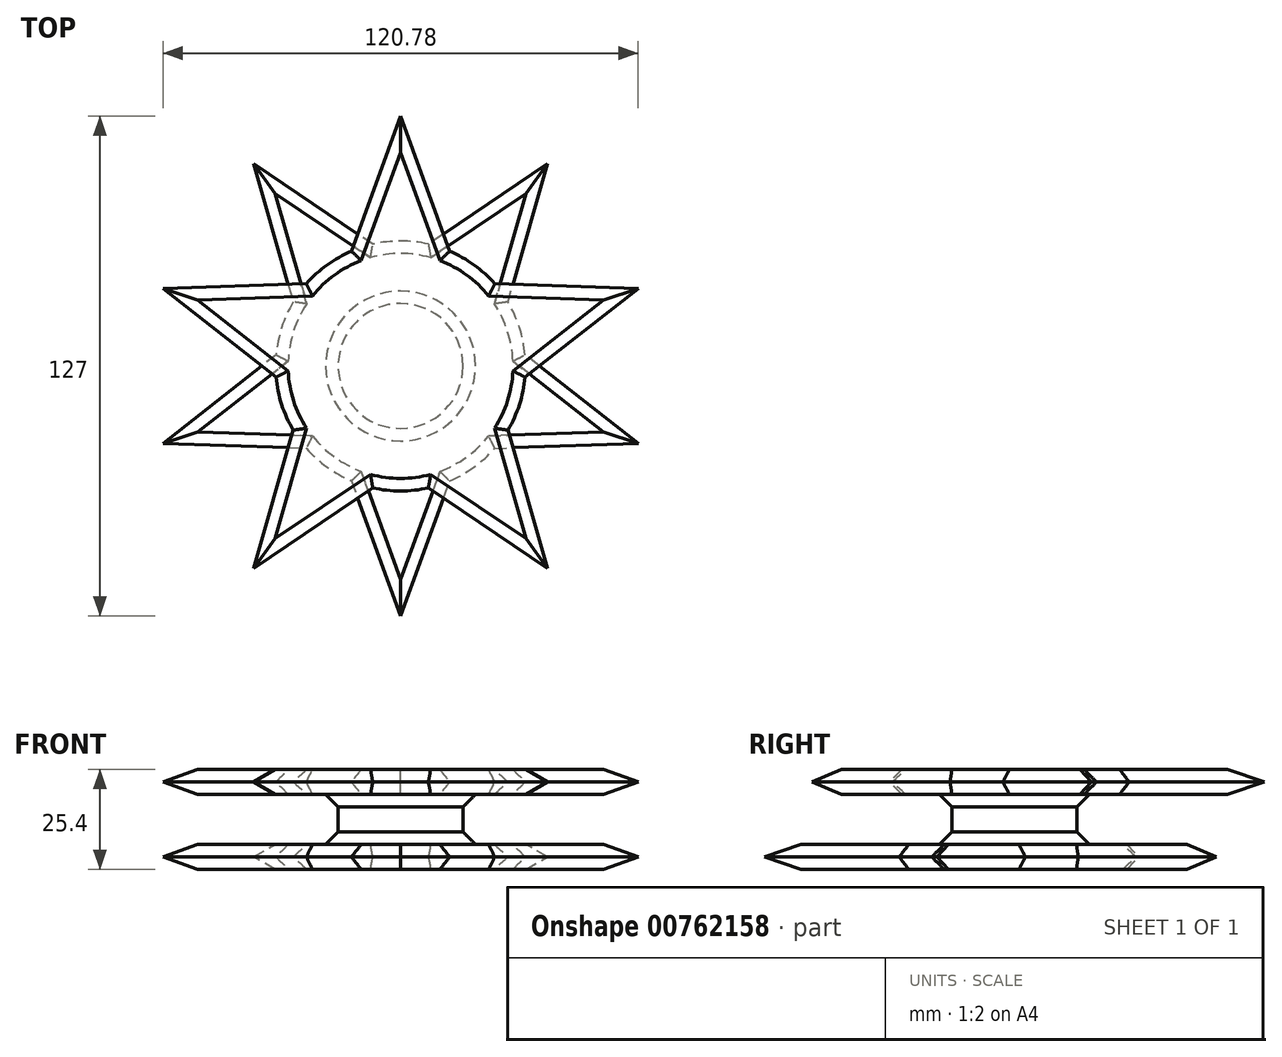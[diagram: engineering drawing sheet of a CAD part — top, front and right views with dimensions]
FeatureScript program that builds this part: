
annotation { "Feature Type Name" : "Feature", "Feature Type Description" : "" }
export const myFeature = defineFeature(function(context is Context, id is Id, definition is map)
    precondition{}
    {
        {
            var Q0;
            Q0=qCreatedBy(makeId("Top.planeOp"),FACE);
            var sketch = newSketch(context, id + "F0", { "sketchPlane" : qUnion([Q0])});
            skCircle(sketch, "E0", {"center": v(0, 0) * mm, "radius": 31.75 * mm});
            skSolve(sketch);
        }
        {
            var Q0;
            Q0 = qSketchRegion(id + "F0", true);
            extrude(context, id + "F1", {"entities" : qUnion([Q0]), "endBound" : BoundingType.SYMMETRIC, "depth" : 25.4 * mm, "offsetDistance" : 25.4 * mm});
        }
        {
            var Q0;
            Q0=qCreatedBy(makeId("Front.planeOp"),FACE);
            var sketch = newSketch(context, id + "F2", { "sketchPlane" : qUnion([Q0])});
            skLineSegment(sketch, "E1", {"start": v(15.88, 6.35) * mm, "end": v(31.75, 6.35) * mm});
            skLineSegment(sketch, "E2.MirrorCS", {"start": v(15.88, -6.35) * mm, "end": v(31.75, -6.35) * mm});
            skLineSegment(sketch, "E3", {"start": v(15.88, 6.35) * mm, "end": v(15.88, -6.35) * mm});
            skPoint(sketch, "E4.orphan", {"position": v(0, -6.35) * mm});
            skPoint(sketch, "E5.MirrorCS.start.orphan", {"position": v(0, 0) * mm});
            skPoint(sketch, "E6.end.orphan", {"position": v(0, 6.35) * mm});
            skPoint(sketch, "E7.start.orphan", {"position": v(31.75, 0) * mm});
            skPoint(sketch, "E8.orphan", {"position": v(31.75, 12.7) * mm});
            skPoint(sketch, "E9.orphan", {"position": v(31.75, -12.7) * mm});
            skLineSegment(sketch, "E10", {"start": v(31.75, 6.35) * mm, "end": v(33.28, 6.35) * mm});
            skLineSegment(sketch, "E11", {"start": v(33.28, 6.35) * mm, "end": v(33.28, -6.35) * mm});
            skLineSegment(sketch, "E12", {"start": v(33.28, -6.35) * mm, "end": v(31.75, -6.35) * mm});
            skLineSegment(sketch, "E13", {"start": v(0, 0) * mm, "end": v(0, 6.35) * mm});
            skSolve(sketch);
        }
        {
            var Q0;
            Q0 = qSketchRegion(id + "F2", true);
            var Q1;
            Q1=sQuery(id+"F2.wireOp",EDGE,"E13");
            revolve(context, id + "F3", {"operationType" : NewBodyOperationType.REMOVE, "surfaceOperationType" : NewSurfaceOperationType.NEW, "entities" : qUnion([Q0]), "axis" : qUnion([Q1]), "revolveType" : RevolveType.FULL, "oppositeDirection" : true});
        }
        {
            var Q0;
            Q0=makeQuery(id+"F1.opExtrude","CAP_FACE",FACE,{"disambiguationData":[OSD([sQuery(id+"F0.wireOp",EDGE,"E0")])],"isStart":false});
            var sketch = newSketch(context, id + "F4", { "sketchPlane" : qUnion([Q0])});
            skCircle(sketch, "E14", {"center": v(0, 0) * mm, "radius": 31.75 * mm});
            skLineSegment(sketch, "E15", {"start": v(0, 0) * mm, "end": v(0, 63.5) * mm});
            skLineSegment(sketch, "E16", {"start": v(0, 63.5) * mm, "end": v(-12.49, 29.2) * mm});
            skLineSegment(sketch, "E17", {"start": v(0, 63.5) * mm, "end": v(12.49, 29.2) * mm});
            skLineSegment(sketch, "E18.1.0", {"start": v(-60.4, 19.62) * mm, "end": v(-31.62, -2.86) * mm});
            skLineSegment(sketch, "E18.1.1", {"start": v(-60.4, 19.62) * mm, "end": v(-23.9, 20.9) * mm});
            skLineSegment(sketch, "E18.2.0", {"start": v(-37.32, -51.37) * mm, "end": v(-7.06, -30.96) * mm});
            skLineSegment(sketch, "E18.2.1", {"start": v(-37.32, -51.37) * mm, "end": v(-27.26, -16.28) * mm});
            skLineSegment(sketch, "E18.3.0", {"start": v(37.32, -51.37) * mm, "end": v(27.26, -16.28) * mm});
            skLineSegment(sketch, "E18.3.1", {"start": v(37.32, -51.37) * mm, "end": v(7.06, -30.96) * mm});
            skLineSegment(sketch, "E18.4.0", {"start": v(60.4, 19.62) * mm, "end": v(23.9, 20.9) * mm});
            skLineSegment(sketch, "E18.4.1", {"start": v(60.4, 19.62) * mm, "end": v(31.62, -2.86) * mm});
            skSolve(sketch);
        }
        {
            var Q0;
            {var subQ0=sQuery(id+"F4.wireOp",EDGE,"E17");Q0=makeQuery(id+"F4.imprint","IMPRINT",FACE,{"disambiguationData":[TD([[makeQuery(id+"F4.imprint","IMPRINT",EDGE,{"derivedFrom":subQ0}),-1.0]])]});}
            var Q1;
            {var subQ0=sQuery(id+"F4.wireOp",EDGE,"E16");Q1=makeQuery(id+"F4.imprint","IMPRINT",FACE,{"disambiguationData":[TD([[makeQuery(id+"F4.imprint","IMPRINT",EDGE,{"derivedFrom":subQ0}),1.0]])]});}
            var Q2;
            {var subQ0=sQuery(id+"F4.wireOp",EDGE,"E18.1.0");Q2=makeQuery(id+"F4.imprint","IMPRINT",FACE,{"disambiguationData":[TD([[makeQuery(id+"F4.imprint","IMPRINT",EDGE,{"derivedFrom":subQ0}),1.0]])]});}
            var Q3;
            {var subQ0=sQuery(id+"F4.wireOp",EDGE,"E18.2.0");Q3=makeQuery(id+"F4.imprint","IMPRINT",FACE,{"disambiguationData":[TD([[makeQuery(id+"F4.imprint","IMPRINT",EDGE,{"derivedFrom":subQ0}),1.0]])]});}
            var Q4;
            {var subQ0=sQuery(id+"F4.wireOp",EDGE,"E18.3.0");Q4=makeQuery(id+"F4.imprint","IMPRINT",FACE,{"disambiguationData":[TD([[makeQuery(id+"F4.imprint","IMPRINT",EDGE,{"derivedFrom":subQ0}),1.0]])]});}
            var Q5;
            {var subQ0=sQuery(id+"F4.wireOp",EDGE,"E18.4.0");Q5=makeQuery(id+"F4.imprint","IMPRINT",FACE,{"disambiguationData":[TD([[makeQuery(id+"F4.imprint","IMPRINT",EDGE,{"derivedFrom":subQ0}),1.0]])]});}
            extrude(context, id + "F5", {"entities" : qUnion([Q0, Q1, Q2, Q3, Q4, Q5]), "operationType" : NewBodyOperationType.ADD, "oppositeDirection" : true, "depth" : 6.35 * mm, "offsetDistance" : 25.4 * mm});
        }
        {
            var Q0;
            Q0=makeQuery(id+"F1.opExtrude","CAP_FACE",FACE,{"disambiguationData":[OSD([sQuery(id+"F0.wireOp",EDGE,"E0")])],"isStart":true});
            var sketch = newSketch(context, id + "F6", { "sketchPlane" : qUnion([Q0])});
            skCircle(sketch, "E19.0", {"center": v(0, 0) * mm, "radius": 31.75 * mm});
            skLineSegment(sketch, "E20", {"start": v(0, 0) * mm, "end": v(0, 63.5) * mm});
            skLineSegment(sketch, "E21", {"start": v(0, 63.5) * mm, "end": v(-12.49, 29.2) * mm});
            skLineSegment(sketch, "E22", {"start": v(0, 63.5) * mm, "end": v(12.49, 29.2) * mm});
            skLineSegment(sketch, "E23.1.0", {"start": v(-60.4, 19.62) * mm, "end": v(-31.62, -2.86) * mm});
            skLineSegment(sketch, "E23.1.1", {"start": v(-60.4, 19.62) * mm, "end": v(-23.9, 20.9) * mm});
            skLineSegment(sketch, "E23.2.0", {"start": v(-37.32, -51.37) * mm, "end": v(-7.06, -30.96) * mm});
            skLineSegment(sketch, "E23.2.1", {"start": v(-37.32, -51.37) * mm, "end": v(-27.26, -16.28) * mm});
            skLineSegment(sketch, "E23.3.0", {"start": v(37.32, -51.37) * mm, "end": v(27.26, -16.28) * mm});
            skLineSegment(sketch, "E23.3.1", {"start": v(37.32, -51.37) * mm, "end": v(7.06, -30.96) * mm});
            skLineSegment(sketch, "E23.4.0", {"start": v(60.4, 19.62) * mm, "end": v(23.9, 20.9) * mm});
            skLineSegment(sketch, "E23.4.1", {"start": v(60.4, 19.62) * mm, "end": v(31.62, -2.86) * mm});
            skSolve(sketch);
        }
        {
            var Q0;
            {var subQ0=sQuery(id+"F6.wireOp",EDGE,"E21");Q0=makeQuery(id+"F6.imprint","IMPRINT",FACE,{"disambiguationData":[TD([[makeQuery(id+"F6.imprint","IMPRINT",EDGE,{"derivedFrom":subQ0}),1.0]])]});}
            var Q1;
            {var subQ0=sQuery(id+"F6.wireOp",EDGE,"E22");Q1=makeQuery(id+"F6.imprint","IMPRINT",FACE,{"disambiguationData":[TD([[makeQuery(id+"F6.imprint","IMPRINT",EDGE,{"derivedFrom":subQ0}),-1.0]])]});}
            var Q2;
            {var subQ0=sQuery(id+"F6.wireOp",EDGE,"E23.1.0");Q2=makeQuery(id+"F6.imprint","IMPRINT",FACE,{"disambiguationData":[TD([[makeQuery(id+"F6.imprint","IMPRINT",EDGE,{"derivedFrom":subQ0}),1.0]])]});}
            var Q3;
            {var subQ0=sQuery(id+"F6.wireOp",EDGE,"E23.4.0");Q3=makeQuery(id+"F6.imprint","IMPRINT",FACE,{"disambiguationData":[TD([[makeQuery(id+"F6.imprint","IMPRINT",EDGE,{"derivedFrom":subQ0}),1.0]])]});}
            var Q4;
            {var subQ0=sQuery(id+"F6.wireOp",EDGE,"E23.2.0");Q4=makeQuery(id+"F6.imprint","IMPRINT",FACE,{"disambiguationData":[TD([[makeQuery(id+"F6.imprint","IMPRINT",EDGE,{"derivedFrom":subQ0}),1.0]])]});}
            var Q5;
            {var subQ0=sQuery(id+"F6.wireOp",EDGE,"E23.3.0");Q5=makeQuery(id+"F6.imprint","IMPRINT",FACE,{"disambiguationData":[TD([[makeQuery(id+"F6.imprint","IMPRINT",EDGE,{"derivedFrom":subQ0}),1.0]])]});}
            extrude(context, id + "F7", {"entities" : qUnion([Q0, Q1, Q2, Q3, Q4, Q5]), "operationType" : NewBodyOperationType.ADD, "oppositeDirection" : true, "depth" : 6.35 * mm, "offsetDistance" : 25.4 * mm});
        }
        {
            var Q0;
            {var subQ0=sQuery(id+"F4.wireOp",EDGE,"E14");Q0=makeQuery(id+"F5.boolean.opBoolean","MERGE",FACE,{"derivedFrom":[makeQuery(id+"F1.opExtrude","CAP_FACE",FACE,{"disambiguationData":[OSD([sQuery(id+"F0.wireOp",EDGE,"E0")])],"isStart":false}),makeQuery(id+"F5.opExtrude","CAP_FACE",FACE,{"disambiguationData":[OSD([subQ0,sQuery(id+"F4.wireOp",EDGE,"E16"),sQuery(id+"F4.wireOp",EDGE,"E17")])],"isStart":true}),makeQuery(id+"F5.opExtrude","CAP_FACE",FACE,{"disambiguationData":[OSD([subQ0,sQuery(id+"F4.wireOp",EDGE,"E18.1.0"),sQuery(id+"F4.wireOp",EDGE,"E18.1.1")])],"isStart":true}),makeQuery(id+"F5.opExtrude","CAP_FACE",FACE,{"disambiguationData":[OSD([subQ0,sQuery(id+"F4.wireOp",EDGE,"E18.2.0"),sQuery(id+"F4.wireOp",EDGE,"E18.2.1")])],"isStart":true}),makeQuery(id+"F5.opExtrude","CAP_FACE",FACE,{"disambiguationData":[OSD([subQ0,sQuery(id+"F4.wireOp",EDGE,"E18.3.0"),sQuery(id+"F4.wireOp",EDGE,"E18.3.1")])],"isStart":true}),makeQuery(id+"F5.opExtrude","CAP_FACE",FACE,{"disambiguationData":[OSD([subQ0,sQuery(id+"F4.wireOp",EDGE,"E18.4.0"),sQuery(id+"F4.wireOp",EDGE,"E18.4.1")])],"isStart":true})]});}
            var Q1;
            {var subQ0=sQuery(id+"F6.wireOp",EDGE,"E19.0");Q1=makeQuery(id+"F7.boolean.opBoolean","MERGE",FACE,{"derivedFrom":[makeQuery(id+"F3.boolean.opBoolean","COPY",FACE,{"derivedFrom":makeQuery(id+"F3.opRevolve","SWEPT_FACE",FACE,{"disambiguationData":[OSD([sQuery(id+"F2.wireOp",EDGE,"E2.MirrorCS"),sQuery(id+"F2.wireOp",EDGE,"E12")])]})}),makeQuery(id+"F7.opExtrude","CAP_FACE",FACE,{"disambiguationData":[OSD([subQ0,sQuery(id+"F6.wireOp",EDGE,"E23.3.0"),sQuery(id+"F6.wireOp",EDGE,"E23.3.1")])],"isStart":false}),makeQuery(id+"F7.opExtrude","CAP_FACE",FACE,{"disambiguationData":[OSD([subQ0,sQuery(id+"F6.wireOp",EDGE,"E23.2.0"),sQuery(id+"F6.wireOp",EDGE,"E23.2.1")])],"isStart":false}),makeQuery(id+"F7.opExtrude","CAP_FACE",FACE,{"disambiguationData":[OSD([subQ0,sQuery(id+"F6.wireOp",EDGE,"E23.1.0"),sQuery(id+"F6.wireOp",EDGE,"E23.1.1")])],"isStart":false}),makeQuery(id+"F7.opExtrude","CAP_FACE",FACE,{"disambiguationData":[OSD([subQ0,sQuery(id+"F6.wireOp",EDGE,"E21"),sQuery(id+"F6.wireOp",EDGE,"E22")])],"isStart":false}),makeQuery(id+"F7.opExtrude","CAP_FACE",FACE,{"disambiguationData":[OSD([subQ0,sQuery(id+"F6.wireOp",EDGE,"E23.4.0"),sQuery(id+"F6.wireOp",EDGE,"E23.4.1")])],"isStart":false})]});}
            var Q2;
            {var subQ0=sQuery(id+"F4.wireOp",EDGE,"E14");Q2=makeQuery(id+"F5.boolean.opBoolean","MERGE",FACE,{"derivedFrom":[makeQuery(id+"F3.boolean.opBoolean","COPY",FACE,{"derivedFrom":makeQuery(id+"F3.opRevolve","SWEPT_FACE",FACE,{"disambiguationData":[OSD([sQuery(id+"F2.wireOp",EDGE,"E1"),sQuery(id+"F2.wireOp",EDGE,"E10")])]})}),makeQuery(id+"F5.opExtrude","CAP_FACE",FACE,{"disambiguationData":[OSD([subQ0,sQuery(id+"F4.wireOp",EDGE,"E16"),sQuery(id+"F4.wireOp",EDGE,"E17")])],"isStart":false}),makeQuery(id+"F5.opExtrude","CAP_FACE",FACE,{"disambiguationData":[OSD([subQ0,sQuery(id+"F4.wireOp",EDGE,"E18.1.0"),sQuery(id+"F4.wireOp",EDGE,"E18.1.1")])],"isStart":false}),makeQuery(id+"F5.opExtrude","CAP_FACE",FACE,{"disambiguationData":[OSD([subQ0,sQuery(id+"F4.wireOp",EDGE,"E18.2.0"),sQuery(id+"F4.wireOp",EDGE,"E18.2.1")])],"isStart":false}),makeQuery(id+"F5.opExtrude","CAP_FACE",FACE,{"disambiguationData":[OSD([subQ0,sQuery(id+"F4.wireOp",EDGE,"E18.3.0"),sQuery(id+"F4.wireOp",EDGE,"E18.3.1")])],"isStart":false}),makeQuery(id+"F5.opExtrude","CAP_FACE",FACE,{"disambiguationData":[OSD([subQ0,sQuery(id+"F4.wireOp",EDGE,"E18.4.0"),sQuery(id+"F4.wireOp",EDGE,"E18.4.1")])],"isStart":false})]});}
            var Q3;
            {var subQ0=sQuery(id+"F6.wireOp",EDGE,"E19.0");Q3=makeQuery(id+"F7.boolean.opBoolean","MERGE",FACE,{"derivedFrom":[makeQuery(id+"F1.opExtrude","CAP_FACE",FACE,{"disambiguationData":[OSD([sQuery(id+"F0.wireOp",EDGE,"E0")])],"isStart":true}),makeQuery(id+"F7.opExtrude","CAP_FACE",FACE,{"disambiguationData":[OSD([subQ0,sQuery(id+"F6.wireOp",EDGE,"E23.3.0"),sQuery(id+"F6.wireOp",EDGE,"E23.3.1")])],"isStart":true}),makeQuery(id+"F7.opExtrude","CAP_FACE",FACE,{"disambiguationData":[OSD([subQ0,sQuery(id+"F6.wireOp",EDGE,"E23.2.0"),sQuery(id+"F6.wireOp",EDGE,"E23.2.1")])],"isStart":true}),makeQuery(id+"F7.opExtrude","CAP_FACE",FACE,{"disambiguationData":[OSD([subQ0,sQuery(id+"F6.wireOp",EDGE,"E23.1.0"),sQuery(id+"F6.wireOp",EDGE,"E23.1.1")])],"isStart":true}),makeQuery(id+"F7.opExtrude","CAP_FACE",FACE,{"disambiguationData":[OSD([subQ0,sQuery(id+"F6.wireOp",EDGE,"E21"),sQuery(id+"F6.wireOp",EDGE,"E22")])],"isStart":true}),makeQuery(id+"F7.opExtrude","CAP_FACE",FACE,{"disambiguationData":[OSD([subQ0,sQuery(id+"F6.wireOp",EDGE,"E23.4.0"),sQuery(id+"F6.wireOp",EDGE,"E23.4.1")])],"isStart":true})]});}
            chamfer(context, id + "F8", {"entities" : qUnion([Q0, Q1, Q2, Q3]), "width" : 3.17 * mm, "tangentPropagation" : true});
        }
    });
